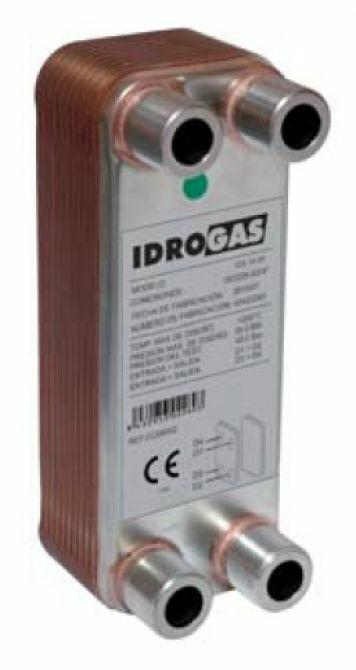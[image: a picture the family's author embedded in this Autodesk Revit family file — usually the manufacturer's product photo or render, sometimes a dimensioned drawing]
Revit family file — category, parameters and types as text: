
# Revit family: IDS14-40_CC08004
name_source: partatom
category: Aparatos eléctricos
revit_build: Autodesk Revit 2016 (Build: 20150220_1215(x64)
units: mm (PartAtom-declared; Revit-internal decimal feet)

## family parameters
Compartido = No
Corte con vacíos al cargar = No
Cota de conector redondo = Diámetro de uso
Mantener orientación de anotación = No
Número OmniClass = 23.80.00.00
Punto de cálculo de habitación = No
Se basa en plano de trabajo = No
Siempre vertical = Sí
Tipo de pieza = Caja de conexiones
Título OmniClass = Electric Power and Lighting

## types (1)
- IDS 14-40
    Caudal máx. = 3,62 m3/h
    Conexiones = 316L acero inox.
    Costo = 0 $
    Código de montaje = CC08004
    Descripción = INTERCAMBIADOR PLACAS TERMOSOLDADO
    Dimensiones = 206 x 78 x ~101 mm
    Fabricante = SALVADOR ESCODA
    Imagen de tipo = IDS-14.jpg
    Material soldadura = 99,99% cobre
    Modelo = IDS 14-40
    Peso = 3 Kg
    Placas = 316L acero inox.
    Placas cubierta = 304 acero inox.
    Presión trabajo = 0-30 bar
    Temperatura máx. trabajo = 225 ºC
    URL = www.salvadorescoda.com
